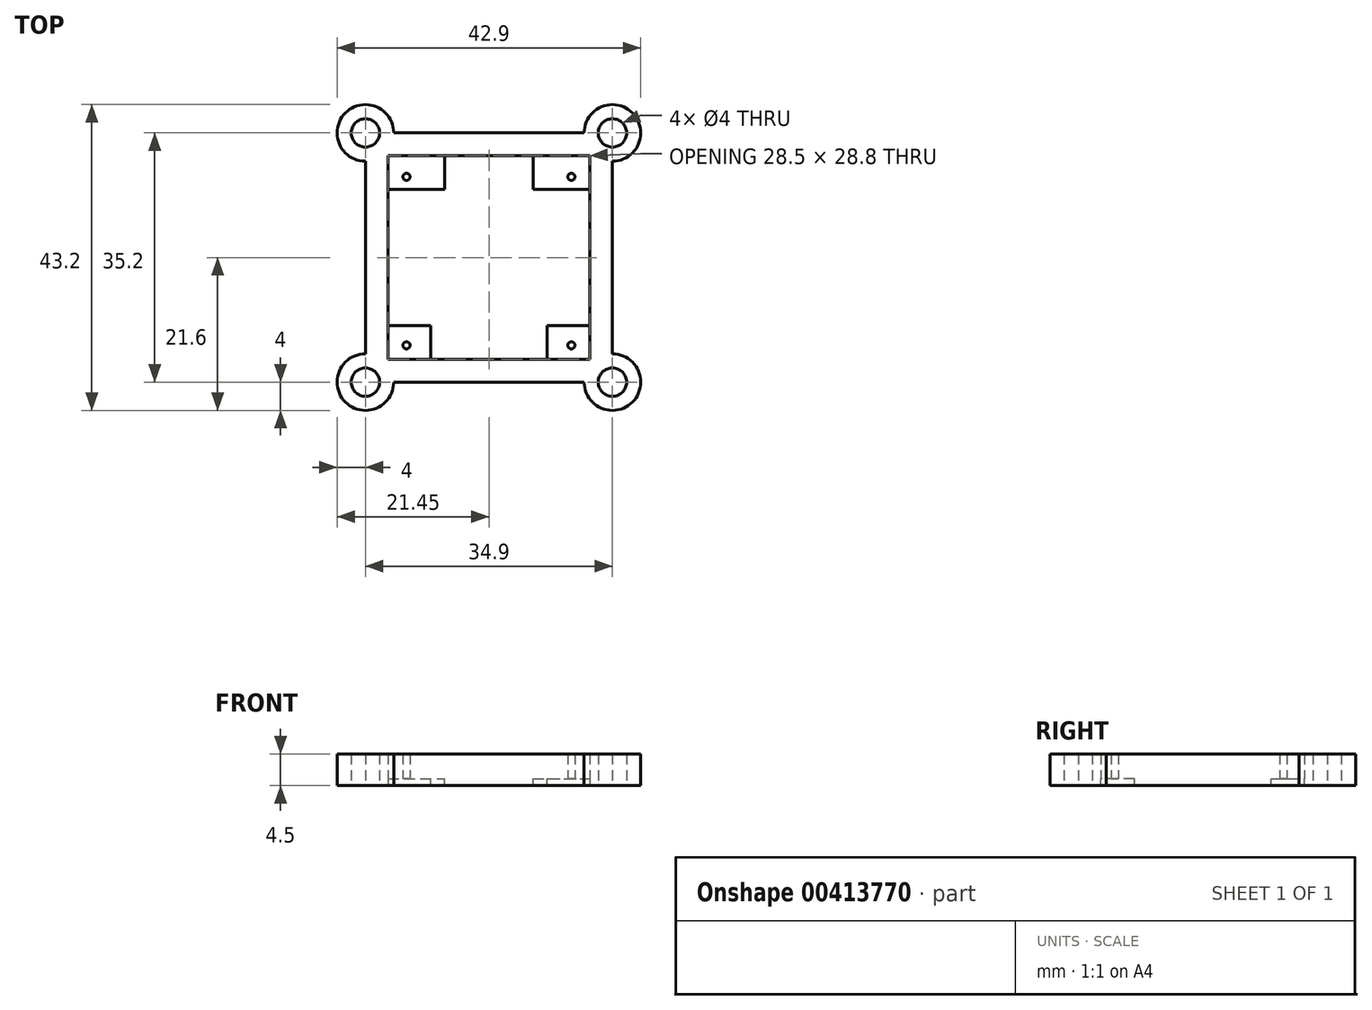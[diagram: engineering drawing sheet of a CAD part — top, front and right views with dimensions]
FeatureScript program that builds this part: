
annotation { "Feature Type Name" : "Feature", "Feature Type Description" : "" }
export const myFeature = defineFeature(function(context is Context, id is Id, definition is map)
    precondition{}
    {
        {
            var Q0;
            Q0=qCreatedBy(makeId("Top.planeOp"),FACE);
            var sketch = newSketch(context, id + "F0", { "sketchPlane" : qUnion([Q0])});
            skLineSegment(sketch, "E0.bottom", {"start": v(-14.25, 14.4) * mm, "end": v(14.25, 14.4) * mm});
            skLineSegment(sketch, "E0.top", {"start": v(-14.25, -14.4) * mm, "end": v(14.25, -14.4) * mm});
            skLineSegment(sketch, "E0.left", {"start": v(-14.25, 14.4) * mm, "end": v(-14.25, -14.4) * mm});
            skLineSegment(sketch, "E0.right", {"start": v(14.25, 14.4) * mm, "end": v(14.25, -14.4) * mm});
            skPoint(sketch, "E0.middle", {"position": v(0, 0) * mm});
            skLineSegment(sketch, "E1.0", {"start": v(17.45, 17.6) * mm, "end": v(17.45, -17.6) * mm});
            skLineSegment(sketch, "E1.1", {"start": v(-17.45, 17.6) * mm, "end": v(17.45, 17.6) * mm});
            skLineSegment(sketch, "E1.2", {"start": v(-17.45, 17.6) * mm, "end": v(-17.45, -17.6) * mm});
            skLineSegment(sketch, "E1.3", {"start": v(-17.45, -17.6) * mm, "end": v(17.45, -17.6) * mm});
            skCircle(sketch, "E2", {"center": v(11.65, -12.4) * mm, "radius": 0.5 * mm});
            skCircle(sketch, "E3", {"center": v(11.65, 11.4) * mm, "radius": 0.5 * mm});
            skCircle(sketch, "E4", {"center": v(-11.65, 11.4) * mm, "radius": 0.5 * mm});
            skCircle(sketch, "E5", {"center": v(-11.65, -12.4) * mm, "radius": 0.5 * mm});
            skLineSegment(sketch, "E6.bottom", {"start": v(-14.25, 9.65) * mm, "end": v(14.25, 9.65) * mm});
            skLineSegment(sketch, "E6.top", {"start": v(-14.25, -9.63) * mm, "end": v(14.25, -9.63) * mm});
            skLineSegment(sketch, "E6.left", {"start": v(-14.25, 9.65) * mm, "end": v(-14.25, -9.63) * mm});
            skLineSegment(sketch, "E6.right", {"start": v(14.25, 9.65) * mm, "end": v(14.25, -9.63) * mm});
            skCircle(sketch, "E7", {"center": v(17.45, 17.6) * mm, "radius": 4 * mm});
            skCircle(sketch, "E8", {"center": v(-17.45, 17.6) * mm, "radius": 4 * mm});
            skCircle(sketch, "E9", {"center": v(-17.45, -17.6) * mm, "radius": 4 * mm});
            skCircle(sketch, "E10", {"center": v(17.45, -17.6) * mm, "radius": 4 * mm});
            skCircle(sketch, "E11", {"center": v(-17.45, 17.6) * mm, "radius": 2 * mm});
            skCircle(sketch, "E12", {"center": v(17.45, 17.6) * mm, "radius": 2 * mm});
            skCircle(sketch, "E13", {"center": v(17.45, -17.6) * mm, "radius": 2 * mm});
            skCircle(sketch, "E14", {"center": v(-17.45, -17.6) * mm, "radius": 2 * mm});
            skSolve(sketch);
        }
        {
            var Q0;
            {var subQ4=sQuery(id+"F0.wireOp",EDGE,"E0.bottom");Q0=makeQuery(id+"F0.imprint","IMPRINT",FACE,{"disambiguationData":[TD([[makeQuery(id+"F0.imprint","IMPRINT",EDGE,{"derivedFrom":subQ4}),1.0]])]});}
            var Q1;
            {var subQ0=sQuery(id+"F0.wireOp",EDGE,"E8");var subQ1=sQuery(id+"F0.wireOp",EDGE,"E1.1");var subQ2=makeQuery(id+"F0.imprint","INTERSECT",VERTEX,{"derivedFrom":[subQ1,subQ0]});Q1=makeQuery(id+"F0.imprint","IMPRINT",FACE,{"disambiguationData":[TD([[makeQuery(id+"F0.imprint","IMPRINT",EDGE,{"disambiguationData":[TD([[subQ2,1.0]])],"derivedFrom":subQ1}),1.0]])]});}
            var Q2;
            {var subQ0=sQuery(id+"F0.wireOp",EDGE,"E7");var subQ1=sQuery(id+"F0.wireOp",EDGE,"E1.0");var subQ2=makeQuery(id+"F0.imprint","INTERSECT",VERTEX,{"derivedFrom":[subQ1,subQ0]});Q2=makeQuery(id+"F0.imprint","IMPRINT",FACE,{"disambiguationData":[TD([[makeQuery(id+"F0.imprint","IMPRINT",EDGE,{"disambiguationData":[TD([[subQ2,1.0]])],"derivedFrom":subQ1}),1.0]])]});}
            var Q3;
            {var subQ0=sQuery(id+"F0.wireOp",EDGE,"E10");var subQ1=sQuery(id+"F0.wireOp",EDGE,"E1.0");var subQ2=makeQuery(id+"F0.imprint","INTERSECT",VERTEX,{"derivedFrom":[subQ1,subQ0]});Q3=makeQuery(id+"F0.imprint","IMPRINT",FACE,{"disambiguationData":[TD([[makeQuery(id+"F0.imprint","IMPRINT",EDGE,{"disambiguationData":[TD([[subQ2,-1.0]])],"derivedFrom":subQ1}),1.0]])]});}
            var Q4;
            {var subQ0=sQuery(id+"F0.wireOp",EDGE,"E9");var subQ1=sQuery(id+"F0.wireOp",EDGE,"E1.2");var subQ2=makeQuery(id+"F0.imprint","INTERSECT",VERTEX,{"derivedFrom":[subQ1,subQ0]});Q4=makeQuery(id+"F0.imprint","IMPRINT",FACE,{"disambiguationData":[TD([[makeQuery(id+"F0.imprint","IMPRINT",EDGE,{"disambiguationData":[TD([[subQ2,-1.0]])],"derivedFrom":subQ1}),-1.0]])]});}
            var Q5;
            {var subQ0=sQuery(id+"F0.wireOp",EDGE,"E8");var subQ1=sQuery(id+"F0.wireOp",EDGE,"E1.1");var subQ2=makeQuery(id+"F0.imprint","INTERSECT",VERTEX,{"derivedFrom":[subQ1,subQ0]});Q5=makeQuery(id+"F0.imprint","IMPRINT",FACE,{"disambiguationData":[TD([[makeQuery(id+"F0.imprint","IMPRINT",EDGE,{"disambiguationData":[TD([[subQ2,1.0]])],"derivedFrom":subQ1}),-1.0]])]});}
            var Q6;
            {var subQ0=sQuery(id+"F0.wireOp",EDGE,"E7");var subQ1=sQuery(id+"F0.wireOp",EDGE,"E1.0");var subQ2=makeQuery(id+"F0.imprint","INTERSECT",VERTEX,{"derivedFrom":[subQ1,subQ0]});Q6=makeQuery(id+"F0.imprint","IMPRINT",FACE,{"disambiguationData":[TD([[makeQuery(id+"F0.imprint","IMPRINT",EDGE,{"disambiguationData":[TD([[subQ2,1.0]])],"derivedFrom":subQ1}),-1.0]])]});}
            var Q7;
            {var subQ0=sQuery(id+"F0.wireOp",EDGE,"E10");var subQ1=sQuery(id+"F0.wireOp",EDGE,"E1.0");var subQ2=makeQuery(id+"F0.imprint","INTERSECT",VERTEX,{"derivedFrom":[subQ1,subQ0]});Q7=makeQuery(id+"F0.imprint","IMPRINT",FACE,{"disambiguationData":[TD([[makeQuery(id+"F0.imprint","IMPRINT",EDGE,{"disambiguationData":[TD([[subQ2,-1.0]])],"derivedFrom":subQ1}),-1.0]])]});}
            var Q8;
            {var subQ0=sQuery(id+"F0.wireOp",EDGE,"E9");var subQ1=sQuery(id+"F0.wireOp",EDGE,"E1.2");var subQ2=makeQuery(id+"F0.imprint","INTERSECT",VERTEX,{"derivedFrom":[subQ1,subQ0]});Q8=makeQuery(id+"F0.imprint","IMPRINT",FACE,{"disambiguationData":[TD([[makeQuery(id+"F0.imprint","IMPRINT",EDGE,{"disambiguationData":[TD([[subQ2,-1.0]])],"derivedFrom":subQ1}),1.0]])]});}
            var Q9;
            Q9=makeQuery(id+"F0.imprint","IMPRINT",FACE,{"disambiguationData":[TD([[makeQuery(id+"F0.imprint","IMPRINT",EDGE,{"derivedFrom":sQuery(id+"F0.wireOp",EDGE,"E4")}),1.0]])]});
            var Q10;
            Q10=makeQuery(id+"F0.imprint","IMPRINT",FACE,{"disambiguationData":[TD([[makeQuery(id+"F0.imprint","IMPRINT",EDGE,{"derivedFrom":sQuery(id+"F0.wireOp",EDGE,"E3")}),1.0]])]});
            var Q11;
            Q11=makeQuery(id+"F0.imprint","IMPRINT",FACE,{"disambiguationData":[TD([[makeQuery(id+"F0.imprint","IMPRINT",EDGE,{"derivedFrom":sQuery(id+"F0.wireOp",EDGE,"E2")}),1.0]])]});
            var Q12;
            Q12=makeQuery(id+"F0.imprint","IMPRINT",FACE,{"disambiguationData":[TD([[makeQuery(id+"F0.imprint","IMPRINT",EDGE,{"derivedFrom":sQuery(id+"F0.wireOp",EDGE,"E5")}),1.0]])]});
            extrude(context, id + "F1", {"entities" : qUnion([Q0, Q1, Q2, Q3, Q4, Q5, Q6, Q7, Q8, Q9, Q10, Q11, Q12]), "depth" : 4.5 * mm, "offsetDistance" : 25 * mm});
        }
        {
            var Q0;
            Q0=qCreatedBy(makeId("Top.planeOp"),FACE);
            var sketch = newSketch(context, id + "F2", { "sketchPlane" : qUnion([Q0])});
            skLineSegment(sketch, "E15.bottom", {"start": v(-14.25, 14.4) * mm, "end": v(14.25, 14.4) * mm});
            skLineSegment(sketch, "E15.top", {"start": v(-14.25, -14.4) * mm, "end": v(14.25, -14.4) * mm});
            skLineSegment(sketch, "E15.left", {"start": v(-14.25, 14.4) * mm, "end": v(-14.25, -14.4) * mm});
            skLineSegment(sketch, "E15.right", {"start": v(14.25, 14.4) * mm, "end": v(14.25, -14.4) * mm});
            skPoint(sketch, "E15.middle", {"position": v(0, 0) * mm});
            skCircle(sketch, "E16", {"center": v(12.25, -12.4) * mm, "radius": 1.75 * mm, "construction": true});
            skCircle(sketch, "E17", {"center": v(11.05, 11.4) * mm, "radius": 1.75 * mm, "construction": true});
            skCircle(sketch, "E18", {"center": v(-12.25, 11.4) * mm, "radius": 1.75 * mm, "construction": true});
            skCircle(sketch, "E19", {"center": v(-11.05, -12.4) * mm, "radius": 1.75 * mm, "construction": true});
            skLineSegment(sketch, "E20.bottom", {"start": v(-14.25, 9.65) * mm, "end": v(14.25, 9.65) * mm});
            skLineSegment(sketch, "E20.top", {"start": v(-14.25, -9.63) * mm, "end": v(14.25, -9.63) * mm});
            skLineSegment(sketch, "E20.left", {"start": v(-14.25, 9.65) * mm, "end": v(-14.25, -9.63) * mm});
            skLineSegment(sketch, "E20.right", {"start": v(14.25, 9.65) * mm, "end": v(14.25, -9.63) * mm});
            skSolve(sketch);
        }
        {
            var Q0;
            {var subQ0=sQuery(id+"F2.wireOp",EDGE,"E15.bottom");Q0=makeQuery(id+"F2.imprint","IMPRINT",FACE,{"disambiguationData":[TD([[makeQuery(id+"F2.imprint","IMPRINT",EDGE,{"derivedFrom":subQ0}),-1.0]])]});}
            var Q1;
            {var subQ0=sQuery(id+"F2.wireOp",EDGE,"E15.top");Q1=makeQuery(id+"F2.imprint","IMPRINT",FACE,{"disambiguationData":[TD([[makeQuery(id+"F2.imprint","IMPRINT",EDGE,{"derivedFrom":subQ0}),1.0]])]});}
            extrude(context, id + "F3", {"entities" : qUnion([Q0, Q1]), "operationType" : NewBodyOperationType.ADD, "depth" : 1 * mm, "offsetDistance" : 25 * mm});
        }
        {
            var Q0;
            Q0=qCreatedBy(makeId("Top.planeOp"),FACE);
            cPlane(context, id + "F4", {"entities" : qUnion([Q0]), "cplaneType" : CPlaneType.OFFSET, "offset" : 3.5 * mm, "width" : 150 * mm, "height" : 150 * mm});
        }
        {
            var Q0;
            Q0=qCreatedBy(id+"F4.planeOp",FACE);
            var sketch = newSketch(context, id + "F5", { "sketchPlane" : qUnion([Q0])});
            skLineSegment(sketch, "E21", {"start": v(-6.25, 27.74) * mm, "end": v(-6.25, -4.9) * mm, "construction": true});
            skLineSegment(sketch, "E22", {"start": v(6.25, 21.83) * mm, "end": v(6.25, 6.4) * mm, "construction": true});
            skLineSegment(sketch, "E23", {"start": v(-8.25, -5.52) * mm, "end": v(-8.25, -18.12) * mm, "construction": true});
            skLineSegment(sketch, "E24", {"start": v(8.25, -5.91) * mm, "end": v(8.25, -17.84) * mm, "construction": true});
            skLineSegment(sketch, "E25.bottom", {"start": v(-6.25, 9.65) * mm, "end": v(6.25, 9.65) * mm});
            skLineSegment(sketch, "E25.top", {"start": v(-6.25, 14.4) * mm, "end": v(6.25, 14.4) * mm});
            skLineSegment(sketch, "E25.left", {"start": v(-6.25, 9.65) * mm, "end": v(-6.25, 14.4) * mm});
            skLineSegment(sketch, "E25.right", {"start": v(6.25, 9.65) * mm, "end": v(6.25, 14.4) * mm});
            skLineSegment(sketch, "E26.bottom", {"start": v(-8.25, -9.63) * mm, "end": v(8.25, -9.63) * mm});
            skLineSegment(sketch, "E26.top", {"start": v(-8.25, -14.4) * mm, "end": v(8.25, -14.4) * mm});
            skLineSegment(sketch, "E26.left", {"start": v(-8.25, -9.63) * mm, "end": v(-8.25, -14.4) * mm});
            skLineSegment(sketch, "E26.right", {"start": v(8.25, -9.63) * mm, "end": v(8.25, -14.4) * mm});
            skSolve(sketch);
        }
        {
            var Q0;
            Q0=qSketchRegion(id+"F5",true);
            extrude(context, id + "F6", {"entities" : qUnion([Q0]), "operationType" : NewBodyOperationType.REMOVE, "oppositeDirection" : true, "depth" : 3.5 * mm, "offsetDistance" : 25 * mm});
        }
    });
